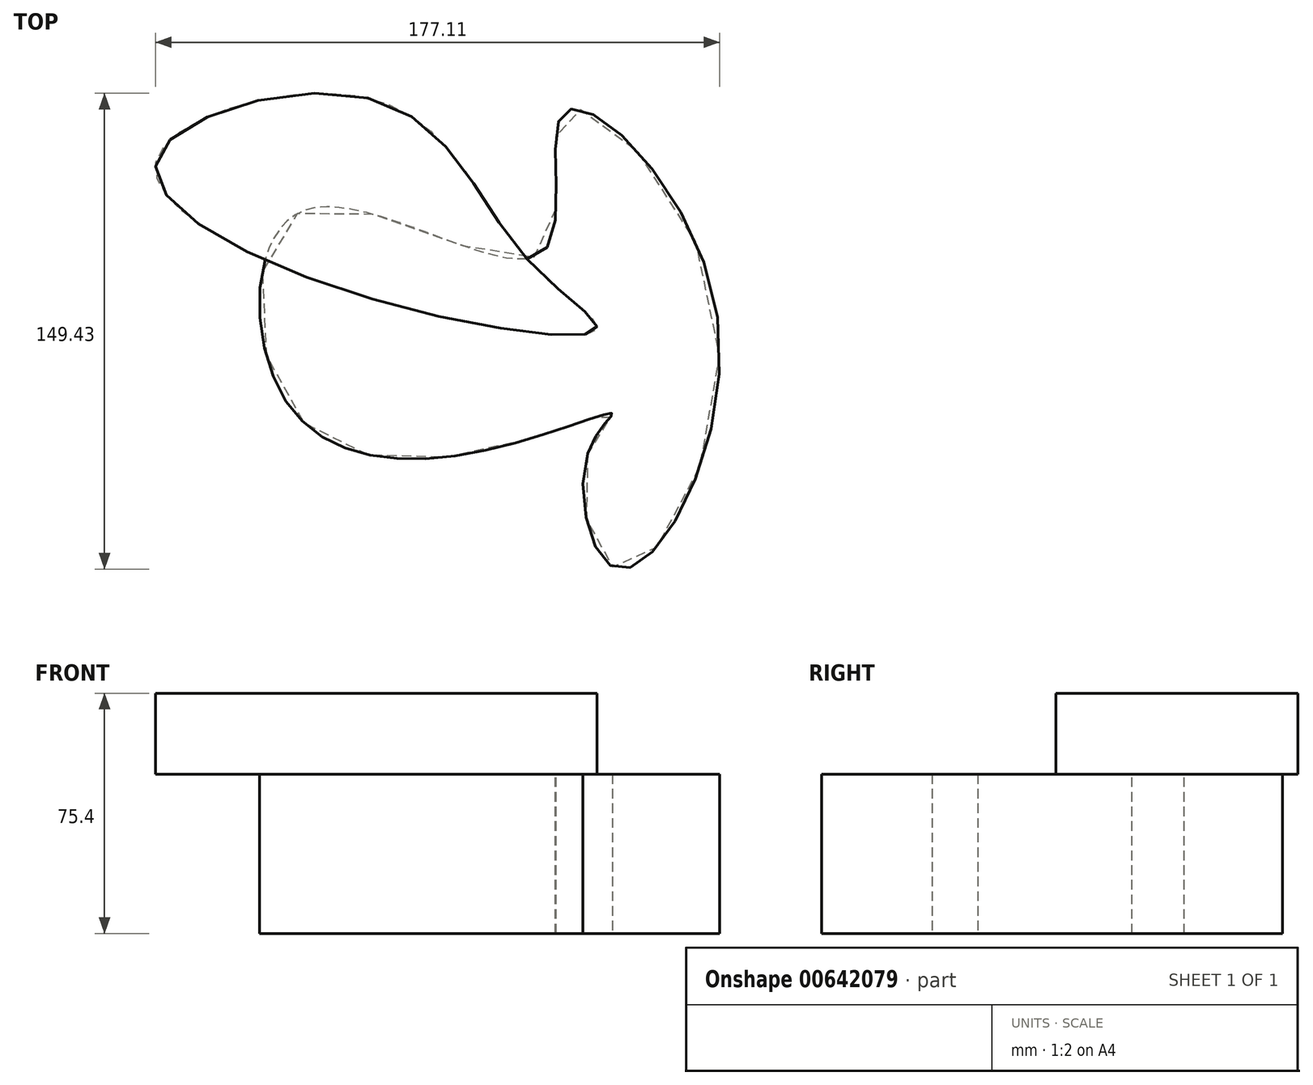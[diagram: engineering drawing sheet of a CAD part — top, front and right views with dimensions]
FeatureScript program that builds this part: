
annotation { "Feature Type Name" : "Feature", "Feature Type Description" : "" }
export const myFeature = defineFeature(function(context is Context, id is Id, definition is map)
    precondition{}
    {
        {
            var Q0;
            Q0=qCreatedBy(makeId("Top.planeOp"),FACE);
            var sketch = newSketch(context, id + "F0", { "sketchPlane" : qUnion([Q0])});
            skFitSpline(sketch, "E0", {"points": [v(36.96, 0) * mm, v(46.56, -36.22) * mm, v(77.24, 45.82) * mm, v(29.2, 106.8) * mm, v(22.54, 62.82) * mm, v(-51.37, 76.5) * mm, v(-58.76, 18.1) * mm, v(0, 0) * mm, v(44.72, 12.56) * mm, v(36.96, 0) * mm]});
            skSolve(sketch);
        }
        {
            var Q0;
            Q0 = qSketchRegion(id + "F0", true);
            extrude(context, id + "F1", {"entities" : qUnion([Q0]), "depth" : 50 * mm, "offsetDistance" : 25.4 * mm});
        }
        {
            var Q0;
            Q0=makeQuery(id+"F1.opExtrude","CAP_FACE",FACE,{"disambiguationData":[OSD([sQuery(id+"F0.wireOp",EDGE,"E0")])],"isStart":false});
            var sketch = newSketch(context, id + "F2", { "sketchPlane" : qUnion([Q0])});
            skFitSpline(sketch, "E1", {"points": [v(17.9, 61.08) * mm, v(39.75, 39.11) * mm, v(-38.43, 50.92) * mm, v(-98.08, 92.87) * mm, v(-28.49, 110.68) * mm, v(17.9, 61.08) * mm]});
            skSolve(sketch);
        }
        {
            var Q0;
            Q0 = qSketchRegion(id + "F2", true);
            extrude(context, id + "F3", {"entities" : qUnion([Q0]), "operationType" : NewBodyOperationType.ADD, "depth" : 25.4 * mm, "offsetDistance" : 25.4 * mm});
        }
    });
